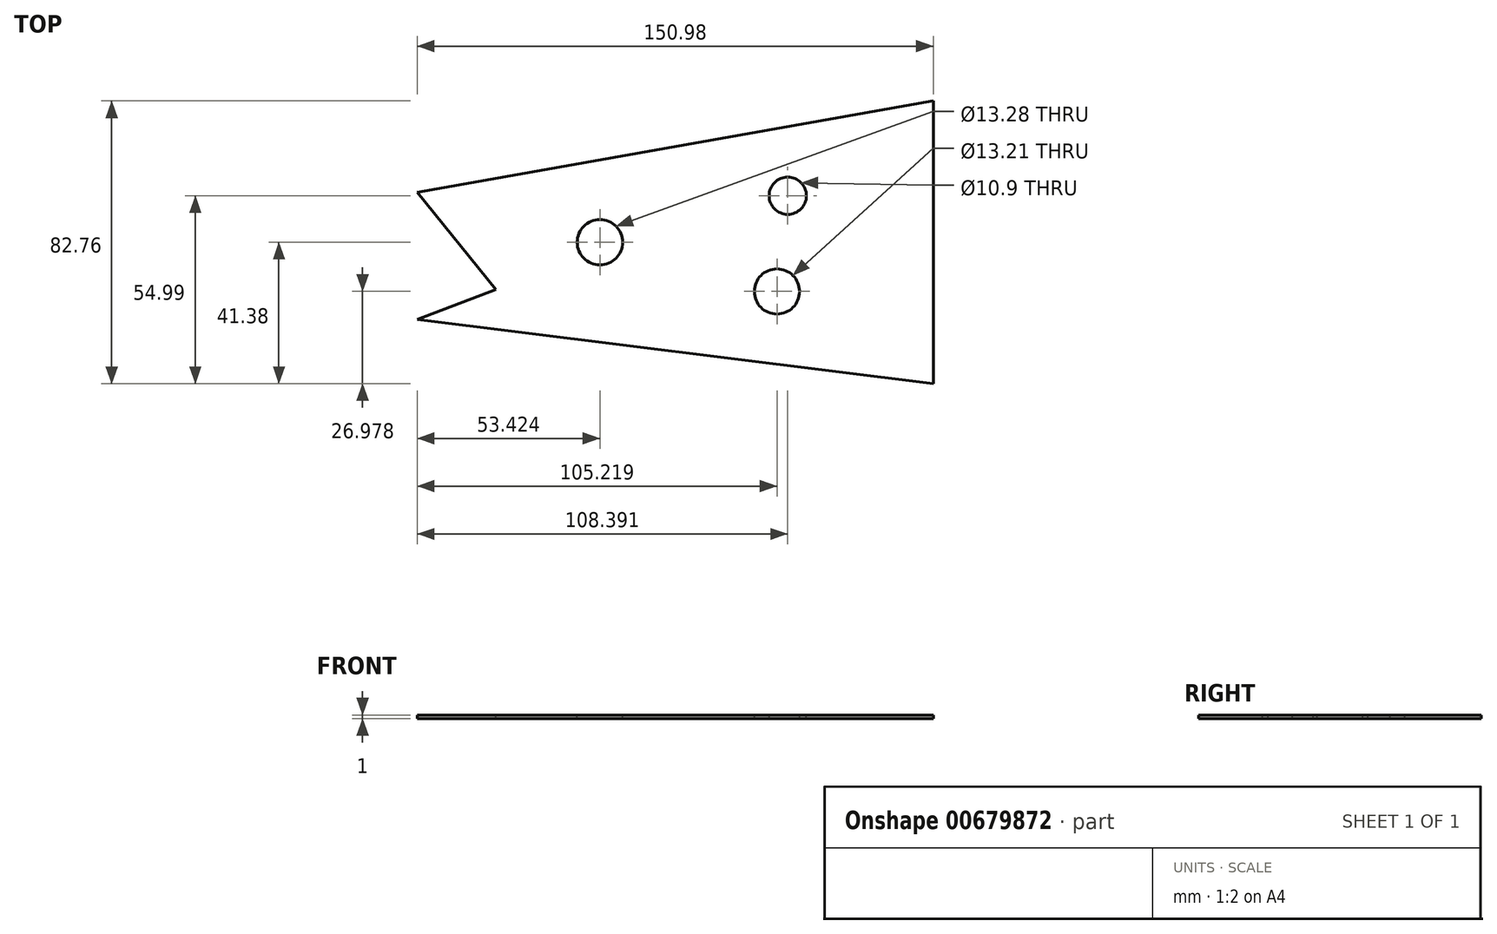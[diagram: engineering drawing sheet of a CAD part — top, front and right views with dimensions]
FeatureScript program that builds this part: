
annotation { "Feature Type Name" : "Feature", "Feature Type Description" : "" }
export const myFeature = defineFeature(function(context is Context, id is Id, definition is map)
    precondition{}
    {
        {
            var Q0;
            Q0=qCreatedBy(makeId("Top.planeOp"),FACE);
            var sketch = newSketch(context, id + "F0", { "sketchPlane" : qUnion([Q0])});
            skLineSegment(sketch, "E0.bottom", {"start": v(-75.49, -41.38) * mm, "end": v(75.49, -41.38) * mm});
            skLineSegment(sketch, "E0.top", {"start": v(-75.49, 41.38) * mm, "end": v(75.49, 41.38) * mm});
            skLineSegment(sketch, "E0.left", {"start": v(-75.49, -41.38) * mm, "end": v(-75.49, 41.38) * mm});
            skLineSegment(sketch, "E0.right", {"start": v(75.49, -41.38) * mm, "end": v(75.49, 41.38) * mm});
            skPoint(sketch, "E0.middle", {"position": v(0, 0) * mm});
            skSolve(sketch);
        }
        {
            var Q0;
            Q0 = qSketchRegion(id + "F0", true);
            extrude(context, id + "F1", {"entities" : qUnion([Q0]), "depth" : 1 * mm, "offsetDistance" : 25.4 * mm});
        }
        {
            var Q0;
            Q0=makeQuery(id+"F1.opExtrude","CAP_FACE",FACE,{"disambiguationData":[OSD([sQuery(id+"F0.wireOp",EDGE,"E0.bottom"),sQuery(id+"F0.wireOp",EDGE,"E0.top"),sQuery(id+"F0.wireOp",EDGE,"E0.left"),sQuery(id+"F0.wireOp",EDGE,"E0.right")])],"isStart":false});
            var sketch = newSketch(context, id + "F2", { "sketchPlane" : qUnion([Q0])});
            skLineSegment(sketch, "E1", {"start": v(75.49, 41.38) * mm, "end": v(-75.49, 14.67) * mm});
            skLineSegment(sketch, "E2", {"start": v(-75.49, 14.67) * mm, "end": v(-52.46, -13.87) * mm});
            skLineSegment(sketch, "E3", {"start": v(-52.46, -13.87) * mm, "end": v(-75.49, -22.6) * mm});
            skLineSegment(sketch, "E4", {"start": v(-75.49, -22.6) * mm, "end": v(75.49, -41.38) * mm});
            skLineSegment(sketch, "E5", {"start": v(75.49, -41.38) * mm, "end": v(-61.7, -59.33) * mm});
            skLineSegment(sketch, "E6", {"start": v(-61.7, -59.33) * mm, "end": v(-118.52, -13.87) * mm});
            skLineSegment(sketch, "E7", {"start": v(-118.52, -13.87) * mm, "end": v(-75.49, 54.3) * mm});
            skLineSegment(sketch, "E8", {"start": v(-75.49, 54.3) * mm, "end": v(72.01, 59.86) * mm});
            skLineSegment(sketch, "E9", {"start": v(72.01, 59.86) * mm, "end": v(75.49, 41.38) * mm});
            skSolve(sketch);
        }
        {
            var Q0;
            {var subQ0=sQuery(id+"F2.wireOp",EDGE,"E1");Q0=makeQuery(id+"F2.imprint","IMPRINT",FACE,{"disambiguationData":[TD([[makeQuery(id+"F2.imprint","IMPRINT",EDGE,{"derivedFrom":subQ0}),-1.0]])]});}
            var Q1;
            {var subQ0=sQuery(id+"F2.wireOp",EDGE,"E2");Q1=makeQuery(id+"F2.imprint","IMPRINT",FACE,{"disambiguationData":[TD([[makeQuery(id+"F2.imprint","IMPRINT",EDGE,{"derivedFrom":subQ0}),-1.0]])]});}
            var Q2;
            {var subQ0=sQuery(id+"F2.wireOp",EDGE,"E4");Q2=makeQuery(id+"F2.imprint","IMPRINT",FACE,{"disambiguationData":[TD([[makeQuery(id+"F2.imprint","IMPRINT",EDGE,{"derivedFrom":subQ0}),-1.0]])]});}
            extrude(context, id + "F3", {"entities" : qUnion([Q0, Q1, Q2]), "operationType" : NewBodyOperationType.REMOVE, "oppositeDirection" : true, "depth" : 25 * mm, "offsetDistance" : 25 * mm});
        }
        {
            var Q0;
            Q0=makeQuery(id+"F1.opExtrude","CAP_FACE",FACE,{"disambiguationData":[OSD([sQuery(id+"F0.wireOp",EDGE,"E0.bottom"),sQuery(id+"F0.wireOp",EDGE,"E0.top"),sQuery(id+"F0.wireOp",EDGE,"E0.left"),sQuery(id+"F0.wireOp",EDGE,"E0.right")])],"isStart":false});
            var sketch = newSketch(context, id + "F4", { "sketchPlane" : qUnion([Q0])});
            skCircle(sketch, "E10", {"center": v(32.9, 13.6) * mm, "radius": 5.45 * mm});
            skCircle(sketch, "E11", {"center": v(29.73, -14.4) * mm, "radius": 6.6 * mm});
            skCircle(sketch, "E12", {"center": v(-22.07, 0) * mm, "radius": 6.64 * mm});
            skSolve(sketch);
        }
        {
            var Q0;
            Q0 = qSketchRegion(id + "F4", true);
            extrude(context, id + "F5", {"entities" : qUnion([Q0]), "operationType" : NewBodyOperationType.REMOVE, "oppositeDirection" : true, "depth" : 25 * mm, "offsetDistance" : 25 * mm});
        }
    });
